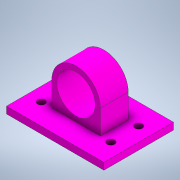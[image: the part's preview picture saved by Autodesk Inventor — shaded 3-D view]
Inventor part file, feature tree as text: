
AUTODESK INVENTOR PART (.ipt)
format: ipt  version: 2022 (Build 260153000, 153)  size: 140,800 bytes
history: native  units: mm
features: sketch x2, extrude x2, hole x1
ambient origin geometry x8: Origin, YZ Plane, XZ Plane, XY Plane, X Axis, Y Axis, Z Axis, Center Point
bodies: Solid1 (feature_tree)
feature tree (5):
  sketch  "Sketch1"  dims[d0=70.0mm d1=50.0mm]
  extrude  "Extrusion1"  Depth=50.0mm
  extrude  "Extrusion2"  Depth=35.0mm
  hole  "Hole2"  [1 undecoded]
  sketch  "Sketch3"  dims[d2=5.0mm d3=0.0mm d13=35.0mm d14=27.5mm d15=20.0mm d16=0.0mm d17=20.0mm d18=20.0mm d19=10.0mm d20=10.0mm d21=5.4mm d22=6.0mm d23=6.0mm d24=2.0mm d25=90.0deg d26=8.0mm d27=20.594885mm]
note: 1 required parameter value undecoded (feature->parameter linkage not recoverable at this tier; creation-order binding heuristic only, values carry confidence <= 0.55)
